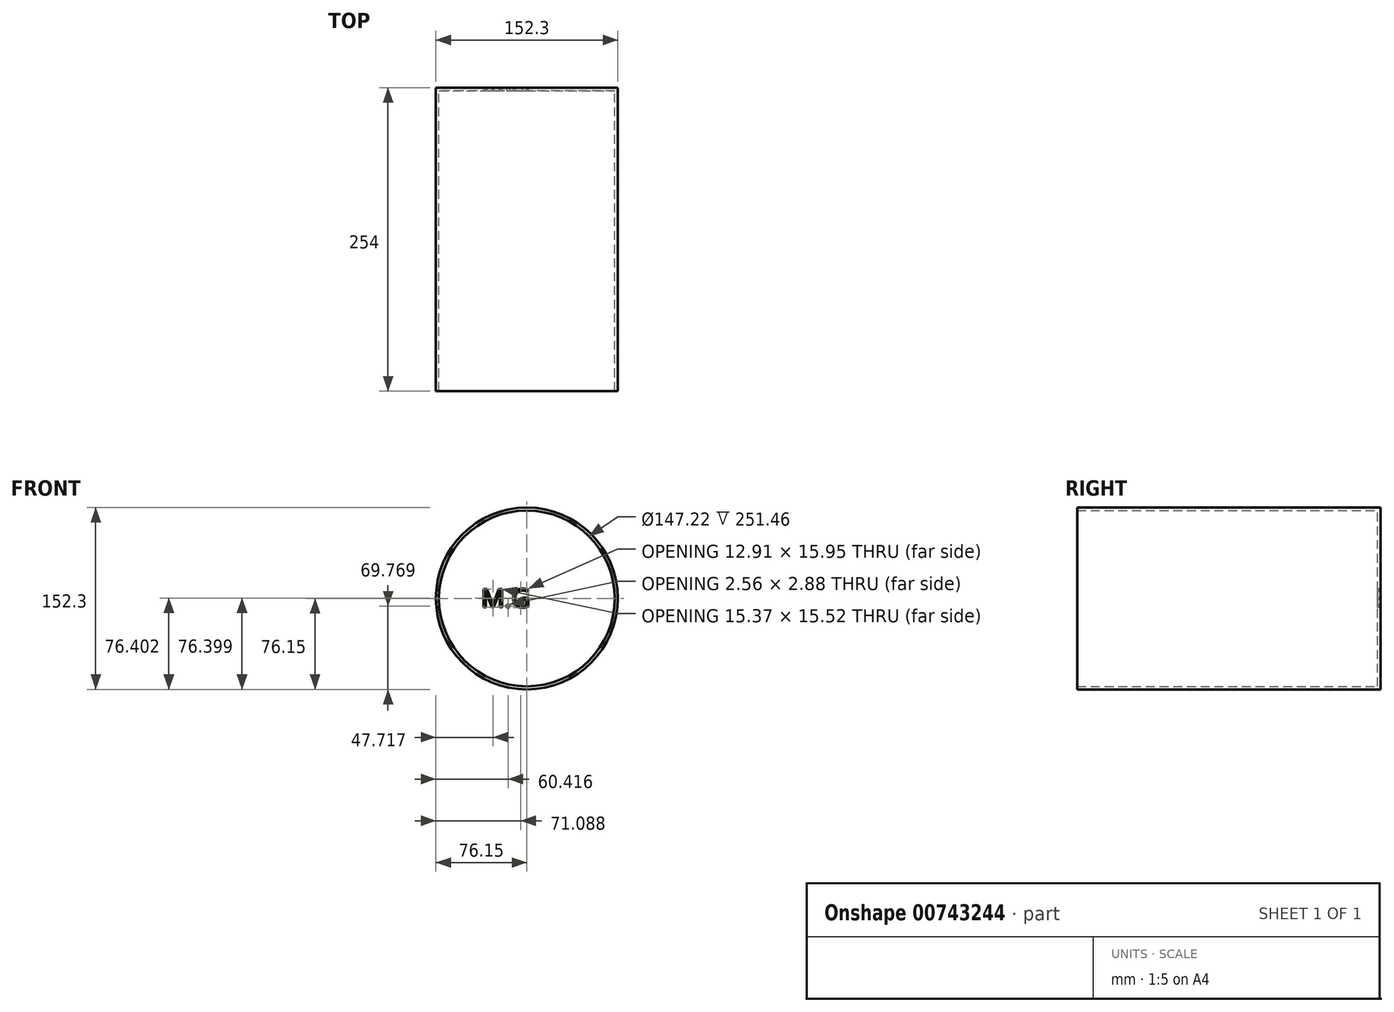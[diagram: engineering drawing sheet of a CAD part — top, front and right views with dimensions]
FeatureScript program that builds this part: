
annotation { "Feature Type Name" : "Feature", "Feature Type Description" : "" }
export const myFeature = defineFeature(function(context is Context, id is Id, definition is map)
    precondition{}
    {
        {
            var Q0;
            Q0=qCreatedBy(makeId("Front.planeOp"),FACE);
            var sketch = newSketch(context, id + "F0", { "sketchPlane" : qUnion([Q0])});
            skCircle(sketch, "E0", {"center": v(0, 0) * mm, "radius": 76.15 * mm});
            skSolve(sketch);
        }
        {
            var Q0;
            Q0 = qSketchRegion(id + "F0", true);
            extrude(context, id + "F1", {"entities" : qUnion([Q0]), "depth" : 254 * mm, "offsetDistance" : 25.4 * mm});
        }
        {
            var Q0;
            Q0=makeQuery(id+"F1.opExtrude","CAP_FACE",FACE,{"disambiguationData":[OSD([sQuery(id+"F0.wireOp",EDGE,"E0")])],"isStart":false});
            shell(context, id + "F2", {"entities" : qUnion([Q0]), "thickness" : 2.54 * mm});
        }
        {
            var Q0;
            {var subQ0=sQuery(id+"F0.wireOp",EDGE,"E0");Q0=makeQuery(id+"F2.opShell","OFFSET_FACE",FACE,{"disambiguationData":[OSD([subQ0]),TDD([makeQuery(id+"F1.opExtrude","CAP_FACE",FACE,{"disambiguationData":[OSD([subQ0])],"isStart":true})])]});}
            var sketch = newSketch(context, id + "F3", { "sketchPlane" : qUnion([Q0])});
            skText(sketch, "E1", { "text": "M.G", "fontName": "OpenSans-Regular.ttf"});
            const initialGuessF3  = {"E1": [-0.03825, -0.00751, 1, 0, 0.01565]};
            skSetInitialGuess(sketch, initialGuessF3);
            skSolve(sketch);
        }
        {
            var Q0;
            Q0 = qSketchRegion(id + "F3", true);
            extrude(context, id + "F4", {"entities" : qUnion([Q0]), "operationType" : NewBodyOperationType.REMOVE, "oppositeDirection" : true, "depth" : 25.4 * mm, "offsetDistance" : 25.4 * mm});
        }
    });
